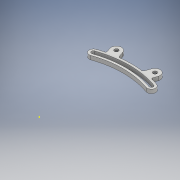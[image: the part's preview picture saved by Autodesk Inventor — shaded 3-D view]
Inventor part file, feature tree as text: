
AUTODESK INVENTOR PART (.ipt)
format: ipt  version: 2017 (Build 210142000, 142)  size: 174,080 bytes
history: native  units: mm
features: sketch x3, extrude x2, hole x1, mirror x1, fillet x1
ambient origin geometry x8: Origin, YZ Plane, XZ Plane, XY Plane, X Axis, Y Axis, Z Axis, Center Point
bodies: Body1 (feature_tree)
feature tree (8):
  sketch  "Sketch3"  dims[d32=153.0mm d33=8.0mm d34=3.25mm d35=45.0mm d36=22.5mm d37=3.0mm d38=8.0mm d39=15.0mm d40=0.0mm d41=71.75mm d42=3.0mm d43=0.0mm]
  extrude  "Extrusion4"  Depth=3.0mm TaperAngle=0.0deg
  extrude  "Extrusion5"  Depth=1.0mm
  hole  "Hole1"  [1 undecoded]
  mirror  "Mirror1"
  fillet  "Fillet1"  [1 undecoded]
  sketch  "Sketch6"  dims[d46=3.0mm d47=0.0mm d48=4.0mm d49=3.0mm d50=6.0mm d51=6.5mm d52=2.0mm d53=90.0deg d54=8.0mm d55=20.594885mm d56=1.0mm]
  sketch  "Sketch5"  dims[d44=3.0mm d45=0.0mm]
note: 2 required parameter values undecoded (feature->parameter linkage not recoverable at this tier; creation-order binding heuristic only, values carry confidence <= 0.55)
